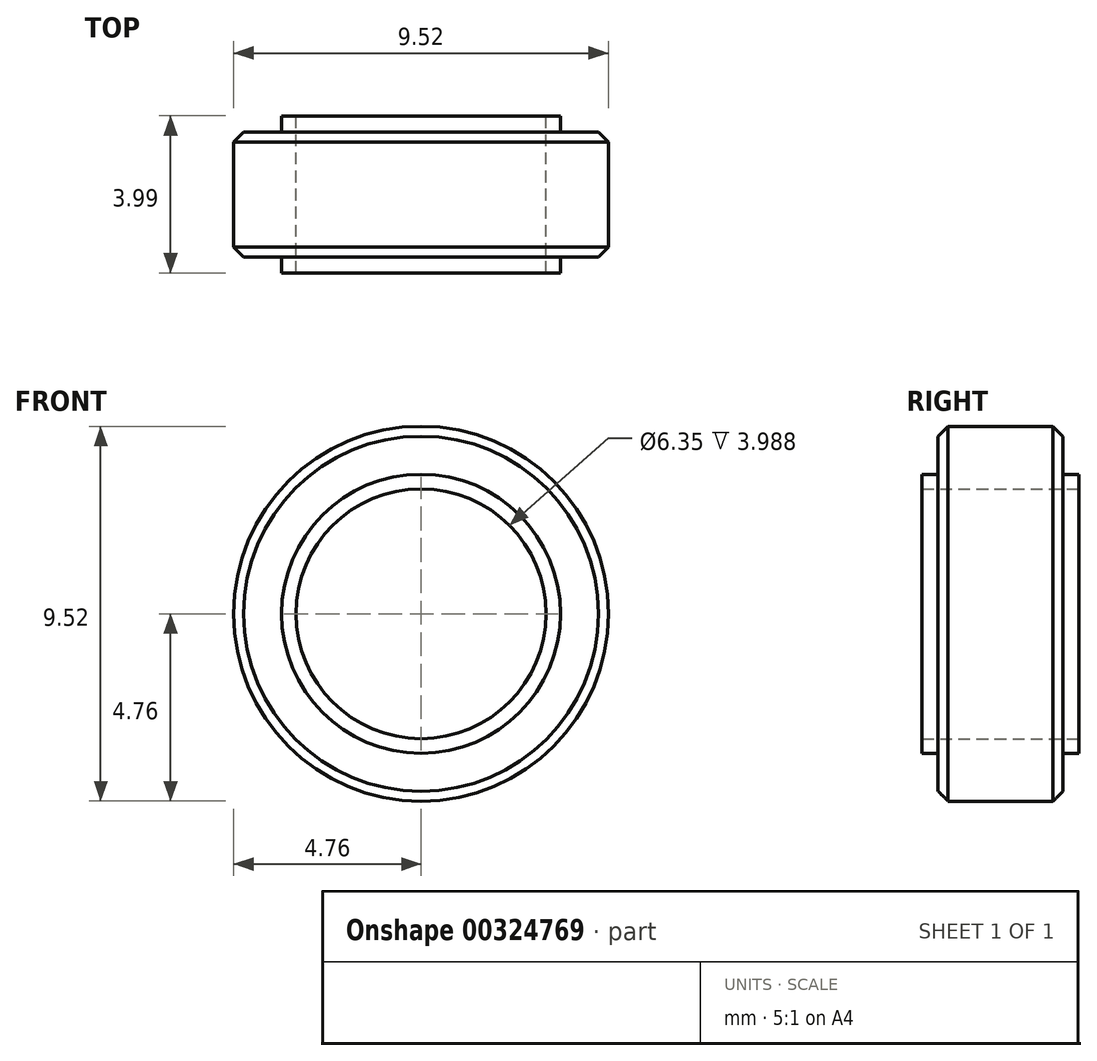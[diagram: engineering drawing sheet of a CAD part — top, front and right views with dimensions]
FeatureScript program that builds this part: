
annotation { "Feature Type Name" : "Feature", "Feature Type Description" : "" }
export const myFeature = defineFeature(function(context is Context, id is Id, definition is map)
    precondition{}
    {
        {
            var Q0;
            Q0=qCreatedBy(makeId("Front.planeOp"),FACE);
            var sketch = newSketch(context, id + "F0", { "sketchPlane" : qUnion([Q0])});
            skCircle(sketch, "E0", {"center": v(0, 0) * mm, "radius": 3.18 * mm});
            skCircle(sketch, "E1", {"center": v(0, 0) * mm, "radius": 4.76 * mm});
            skSolve(sketch);
        }
        {
            var Q0;
            Q0=makeQuery(id+"F0.imprint","IMPRINT",FACE,{"disambiguationData":[TD([[makeQuery(id+"F0.imprint","IMPRINT",EDGE,{"derivedFrom":sQuery(id+"F0.wireOp",EDGE,"E0")}),-1.0]])]});
            extrude(context, id + "F1", {"entities" : qUnion([Q0]), "depth" : 3.17 * mm, "offsetDistance" : 25.4 * mm});
        }
        {
            var Q0;
            Q0=makeQuery(id+"F1.opExtrude","CAP_FACE",FACE,{"disambiguationData":[OSD([sQuery(id+"F0.wireOp",EDGE,"E0"),sQuery(id+"F0.wireOp",EDGE,"E1")])],"isStart":false});
            var sketch = newSketch(context, id + "F2", { "sketchPlane" : qUnion([Q0])});
            skCircle(sketch, "E2", {"center": v(0, 0) * mm, "radius": 3.18 * mm});
            skCircle(sketch, "E3", {"center": v(0, 0) * mm, "radius": 3.54 * mm});
            skSolve(sketch);
        }
        {
            var Q0;
            Q0=makeQuery(id+"F2.imprint","IMPRINT",FACE,{"disambiguationData":[TD([[makeQuery(id+"F2.imprint","IMPRINT",EDGE,{"derivedFrom":sQuery(id+"F2.wireOp",EDGE,"E2")}),-1.0]])]});
            extrude(context, id + "F3", {"entities" : qUnion([Q0]), "operationType" : NewBodyOperationType.ADD, "depth" : 0.4 * mm, "offsetDistance" : 25.4 * mm});
        }
        {
            var Q0;
            Q0=makeQuery(id+"F1.opExtrude","CAP_FACE",FACE,{"disambiguationData":[OSD([sQuery(id+"F0.wireOp",EDGE,"E0"),sQuery(id+"F0.wireOp",EDGE,"E1")])],"isStart":true});
            var sketch = newSketch(context, id + "F4", { "sketchPlane" : qUnion([Q0])});
            skCircle(sketch, "E4", {"center": v(0, 0) * mm, "radius": 3.18 * mm});
            skCircle(sketch, "E5", {"center": v(0, 0) * mm, "radius": 3.54 * mm});
            skSolve(sketch);
        }
        {
            var Q0;
            Q0=makeQuery(id+"F4.imprint","IMPRINT",FACE,{"disambiguationData":[TD([[makeQuery(id+"F4.imprint","IMPRINT",EDGE,{"derivedFrom":sQuery(id+"F4.wireOp",EDGE,"E4")}),1.0]])]});
            extrude(context, id + "F5", {"entities" : qUnion([Q0]), "operationType" : NewBodyOperationType.ADD, "depth" : 0.4 * mm, "offsetDistance" : 25.4 * mm});
        }
        {
            var Q0;
            Q0=makeQuery(id+"F1.opExtrude","CAP_EDGE",EDGE,{"disambiguationData":[OSD([sQuery(id+"F0.wireOp",EDGE,"E1")])],"isStart":false});
            var Q1;
            Q1=makeQuery(id+"F1.opExtrude","CAP_EDGE",EDGE,{"disambiguationData":[OSD([sQuery(id+"F0.wireOp",EDGE,"E1")])],"isStart":true});
            chamfer(context, id + "F6", {"entities" : qUnion([Q0, Q1]), "width" : 0.25 * mm, "tangentPropagation" : true});
        }
    });
